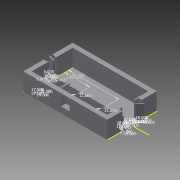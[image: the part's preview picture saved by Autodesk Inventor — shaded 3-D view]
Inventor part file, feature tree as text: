
AUTODESK INVENTOR PART (.ipt)
format: ipt  version: 2013 SP2 (Build 170200200, 200)  size: 413,696 bytes
history: native  units: in
note: dims shown in document units (in); Inventor stores cm internally (conversion verified against a paired STEP export)
features: extrude x19, sketch x12, projected_geometry x2
ambient origin geometry x8: Origin, YZ Plane, XZ Plane, XY Plane, X Axis, Y Axis, Z Axis, Center Point
feature tree (33):
  extrude  "Extrusion9"  Depth=132.0in
  extrude  "Extrusion10"  Depth=216.0in
  extrude  "Extrusion11"  Depth=24.0in
  extrude  "Extrusion12"  Depth=72.0in
  extrude  "Extrusion13"  Depth=24.0in
  extrude  "Extrusion15"  Depth=4.5in
  sketch  "Sketch15"  dims[d34=48.0in d35=114.0in]
  extrude  "Extrusion18"  Depth=168.0in
  extrude  "Extrusion19"  Depth=114.0in
  extrude  "Extrusion20"  Depth=35.0in
  extrude  "Extrusion21"  Depth=468.0in
  extrude  "Extrusion22"  Depth=1.0in TaperAngle=0.0deg
  extrude  "Extrusion23"  Depth=7.5in
  extrude  "Extrusion24"  Depth=7.25in
  extrude  "Extrusion25"  Depth=28.5in
  extrude  "Extrusion26"  Depth=7.5in
  extrude  "Extrusion27"  Depth=7.25in
  extrude  "Extrusion16"  Depth=7.5in
  extrude  "Extrusion17"  Depth=7.25in
  extrude  "Extrusion14"  Depth=7.5in
  sketch  "Sketch1"  dims[d0=288.0in d1=480.0in d2=432.0in d3=240.0in d5=132.0in d7=150.0in]
  sketch  "Sketch8"  dims[d11=57.0in d17=216.0in]
  projected_geometry  "Projected Loop5"
  sketch  "Sketch9"  dims[d18=276.0in d19=24.0in]
  projected_geometry  "Projected Loop6"
  sketch  "Sketch10"  dims[d20=24.0in d23=72.0in]
  sketch  "Sketch11"  dims[d24=102.0in d25=24.0in]
  sketch  "Sketch12"  dims[d27=432.0in d28=4.5in]
  sketch  "Sketch14"  dims[d29=0.0in d30=168.0in]
  sketch  "Sketch16"  dims[d36=24.0in d46=35.0in]
  sketch  "Sketch17"  dims[d105=35.0in d106=468.0in]
  sketch  "Sketch18"  dims[d107=96.0in d108=0.0in d109=1.0in d110=0.0in]
  sketch  "Sketch19"  dims[d111=16.0in d112=0.0in d113=7.5in d115=7.25in d116=28.5in d117=7.5in d118=7.25in d119=7.5in d120=7.25in d121=7.5in d122=7.25in d123=7.5in d124=7.25in d125=7.5in d126=7.25in d127=7.5in d128=7.25in d129=7.5in d130=7.25in d131=7.5in d132=7.25in d133=7.5in d134=7.25in d135=7.5in d136=7.25in d137=7.5in d138=7.25in d139=7.5in d140=7.25in d141=7.5in d142=7.25in d143=16.0in d144=0.0in d145=48.0in d147=48.0in d148=32.0in d150=16.0in d151=0.0in d152=12.75in d153=0.0in d154=7.25in d155=7.5in d156=1.0in d158=1.0in d159=0.0in d161=12.0in d163=12.0in d164=140.0in d165=280.0in d166=12.0in d167=17.5in d168=17.5in d169=12.0in d172=17.0in d173=17.0in d174=8.5in d175=12.0in d176=17.0in d177=17.0in d178=8.5in d179=12.0in d180=17.0in d181=17.0in d182=8.5in d183=18.0in d184=18.0in d185=24.0in d186=2.0in d187=0.0in d188=3.0in d189=0.0in d190=1.0in d191=0.0in d192=6.0in d193=6.0in d194=6.0in d195=18.0in d196=18.0in d197=18.0in d198=18.0in d199=36.0in d200=6.0in d201=1.0in d202=0.0in d203=1.0in d204=0.0in d205=80.0in d206=0.0in d207=80.0in d208=0.0in d209=80.0in d210=0.0in d211=80.0in d212=0.0in d213=1.0in d214=0.0in d215=6.0in d216=36.0in d217=80.0in d218=0.0in d219=1.0in d220=0.0in]
